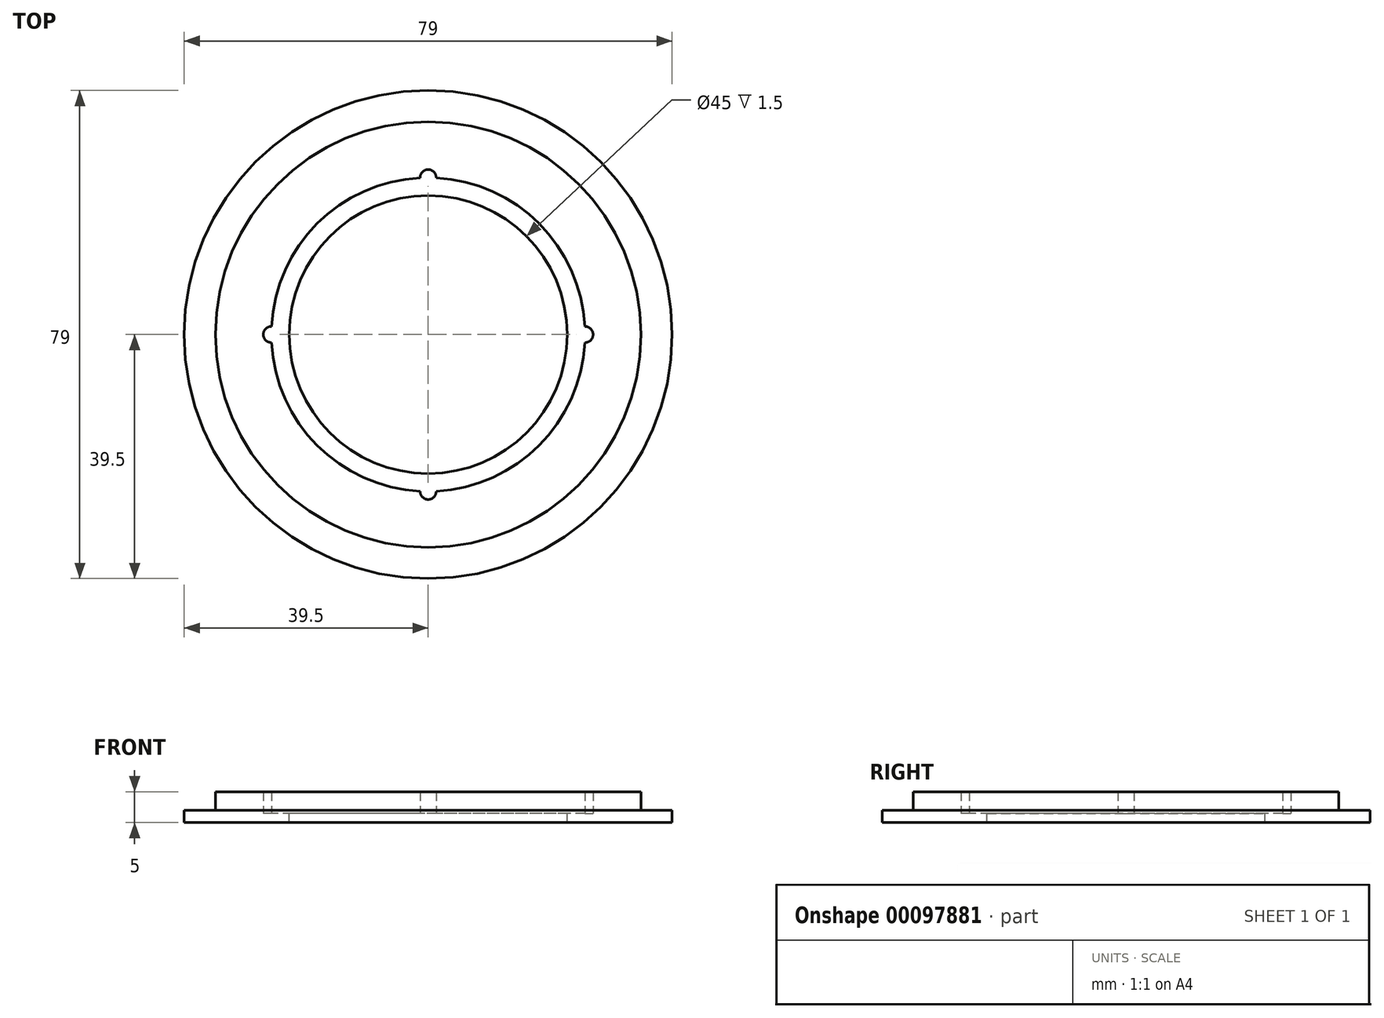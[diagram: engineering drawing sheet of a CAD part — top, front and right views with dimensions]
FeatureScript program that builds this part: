
annotation { "Feature Type Name" : "Feature", "Feature Type Description" : "" }
export const myFeature = defineFeature(function(context is Context, id is Id, definition is map)
    precondition{}
    {
        {
            var Q0;
            Q0=qCreatedBy(makeId("Front.planeOp"),FACE);
            var sketch = newSketch(context, id + "F0", { "sketchPlane" : qUnion([Q0])});
            skLineSegment(sketch, "E0", {"start": v(-39.5, 0) * mm, "end": v(-22.5, 0) * mm});
            skLineSegment(sketch, "E1", {"start": v(-22.5, 0) * mm, "end": v(-22.5, 1.5) * mm});
            skLineSegment(sketch, "E2", {"start": v(-22.5, 1.5) * mm, "end": v(-25.4, 1.5) * mm});
            skLineSegment(sketch, "E3", {"start": v(-25.4, 1.5) * mm, "end": v(-25.4, 5) * mm});
            skLineSegment(sketch, "E4", {"start": v(-25.4, 5) * mm, "end": v(-34.45, 5) * mm});
            skLineSegment(sketch, "E5", {"start": v(-34.45, 5) * mm, "end": v(-34.45, 2) * mm});
            skLineSegment(sketch, "E6", {"start": v(-34.45, 2) * mm, "end": v(-39.5, 2) * mm});
            skLineSegment(sketch, "E7", {"start": v(-39.5, 2) * mm, "end": v(-39.5, 0) * mm});
            skLineSegment(sketch, "E8", {"start": v(0, 24.49) * mm, "end": v(0, -14.91) * mm});
            skSolve(sketch);
        }
        {
            var Q0;
            Q0=makeQuery(id+"F0.imprint","IMPRINT",FACE,{"disambiguationData":[TD([[makeQuery(id+"F0.imprint","IMPRINT",EDGE,{"derivedFrom":sQuery(id+"F0.wireOp",EDGE,"E0")}),1.0]])]});
            var Q1;
            Q1=sQuery(id+"F0.wireOp",EDGE,"E8");
            revolve(context, id + "F1", {"entities" : qUnion([Q0]), "axis" : qUnion([Q1]), "revolveType" : RevolveType.FULL});
        }
        {
            var Q0;
            Q0=qCreatedBy(makeId("Top.planeOp"),FACE);
            var sketch = newSketch(context, id + "F2", { "sketchPlane" : qUnion([Q0])});
            skCircle(sketch, "E9", {"center": v(0, 25.4) * mm, "radius": 1.3 * mm});
            skCircle(sketch, "E10.1.0", {"center": v(-25.4, 0) * mm, "radius": 1.3 * mm});
            skCircle(sketch, "E10.2.0", {"center": v(0, -25.4) * mm, "radius": 1.3 * mm});
            skCircle(sketch, "E10.3.0", {"center": v(25.4, 0) * mm, "radius": 1.3 * mm});
            skPoint(sketch, "E10.center", {"position": v(0, 0) * mm});
            skSolve(sketch);
        }
        {
            var Q0;
            Q0 = qSketchRegion(id + "F2", true);
            extrude(context, id + "F3", {"entities" : qUnion([Q0]), "operationType" : NewBodyOperationType.REMOVE, "depth" : 5 * mm, "hasSecondDirection" : true, "secondDirectionOppositeDirection" : false, "secondDirectionDepth" : 1.5 * mm});
        }
    });
